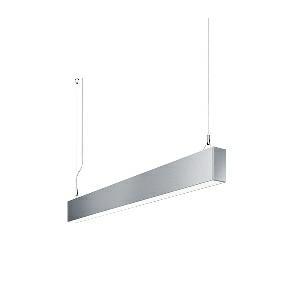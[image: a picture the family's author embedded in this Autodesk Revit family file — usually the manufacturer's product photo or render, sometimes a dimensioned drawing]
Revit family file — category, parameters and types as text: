
# Revit family: idoo_line_-_ilp_2000_830_d_00805716_a1c0
name_source: partatom
category: Lighting Fixtures
units: mm (PartAtom-declared; Revit-internal decimal feet)

## family parameters
Cut with Voids When Loaded = No
Host = Face
Light Source = No
Part Type = Normal
Room Calculation Point = No
Round Connector Dimension = Use Diameter
Shared = No

## types (1)
- IDOO.line - ILP 2000/830/D (1 x LED, 2250 lm, 3000K)
    Apparent Load = 17 VA
    Approval mark = CE
    CIE Flux Codes = 66 91 98 40 100
    Color Rendering = 80-89
    Color Temperature = 3000K
    Control Gear = Electronic ballast
    Default Elevation = 1800 mm
    Description = ILP 2000/830/D|Suspended luminaire|light source: LED|connected load: 220-240 V, 50/60 Hz|Power consumption: approx. 17 W|standby: approx. 0,20|luminous flux: 2250 lm|luminous efficacy: 132 lm/W|light distribution: Direct/indirect|direct ratio: approx. 40 %|colour temperature: Warm white, ca. 3000 K|color rendering index (CRI): >= 80|chromaticity tolerance:  3 SDCM|System of protection: IP 40|technology: Continuously dimmable|luminaire body|material: Sectional aluminium|colour: Silver|lamp cover: Acrylic (PMMA), Clear|mains lead: 2.00 m With free stranded wires|Fastening: Steel cable 0.3 - 0.7 m|glare control: Prism aperture|luminance(L65): <= 2700 cd/m|unified glare rating(4H 8H): <=  16|special features: DALI Load 1x, TouchDIM - dimming via standard switch, Flicker-free, Suitable as emergency lighting|
    Frequency = 50 Hz
    Height = 110 mm
    Lamp = 1 x LED
    Lamp Light Flux = 2250 lm
    Lamp count = 1
    Length = 854 mm
    Luminous efficacy = 132 lm/W
    Manufacturer = Waldmann
    ModVariant = No
    Model = 00805716
    Mounting Place = Ceiling
    Mounting Type = Pendant
    Number of Poles = 1
    OnlyDefault = Yes
    Power Factor = 1
    Product Name = IDOO.line - ILP 2000/830/D
    Product group = Suspended luminaire
    ProductGroupID = 9
    Protection Class = Protection class I
    Protection Degree = IP 40
    RLX_Detail_Level = 1
    RLX_Emergency_Light_Flux = 0 lm
    RLX_Emergency_Type = 0
    RLX_Emergency_Type_DB = No
    RlxData = <blob elided: 19513 chars, md5=e0949158>
    Socket = socket
    Standby Power = 0 W
    System Light Flux = 2250 lm
    System Power = 17 W
    Type Comments = Product without accessories
    Type Image = 113288000-00692512.jpg
    URL = http://relux.com
    VarID = ---
    Voltage = 230 V
    Voltage Range = 220-240 V
    Weight = 0.00 kg
    Width = 60 mm  [stored 0.19685 ft]

note: [stored X ft] marks values corroborated as IEEE doubles in the binary element streams (Revit-internal decimal feet)

## geometry (parser evidence)
native form markers: Blend x4, Sweep x12
no freeform markers — native parametric forms only
